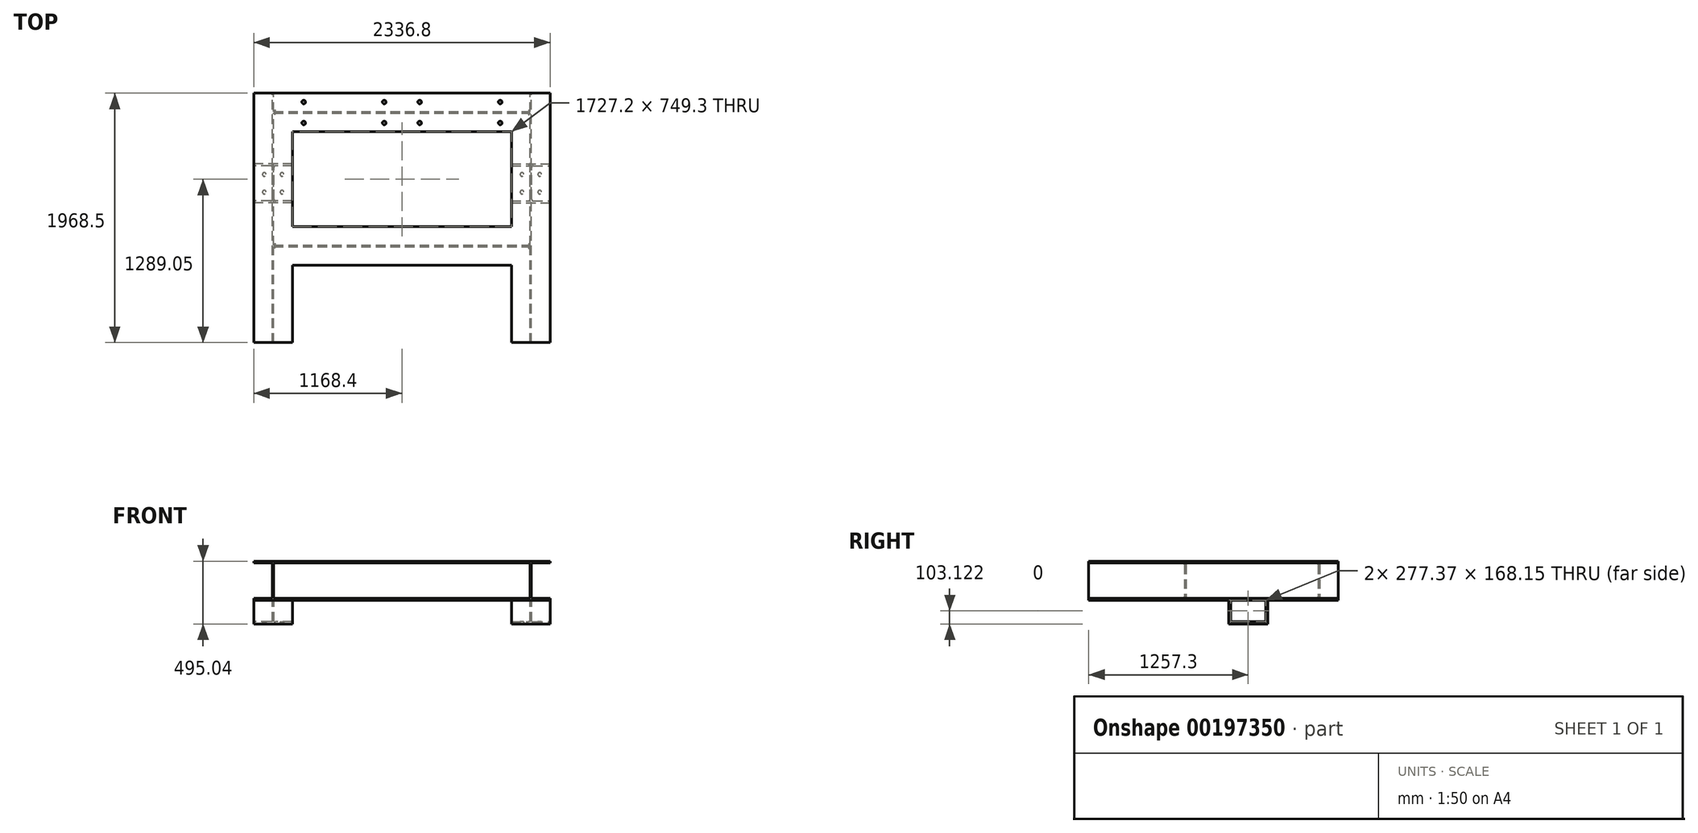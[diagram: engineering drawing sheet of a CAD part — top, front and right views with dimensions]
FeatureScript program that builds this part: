
annotation { "Feature Type Name" : "Feature", "Feature Type Description" : "" }
export const myFeature = defineFeature(function(context is Context, id is Id, definition is map)
    precondition{}
    {
        {
            var Q0;
            Q0=qCreatedBy(makeId("Front.planeOp"),FACE);
            var sketch = newSketch(context, id + "F0", { "sketchPlane" : qUnion([Q0])});
            skLineSegment(sketch, "E0", {"start": v(0, 115.72) * mm, "end": v(0, -109.56) * mm, "construction": true});
            skLineSegment(sketch, "E1", {"start": v(-1016, 0) * mm, "end": v(153.72, 0) * mm, "construction": true});
            skLineSegment(sketch, "E2.0", {"start": v(-1016, 115.72) * mm, "end": v(-1016, -109.56) * mm, "construction": true});
            skPoint(sketch, "E3.orphan", {"position": v(-192.41, 0) * mm});
            skLineSegment(sketch, "E4.bottom", {"start": v(-1168.4, -153.92) * mm, "end": v(-863.6, -153.92) * mm});
            skLineSegment(sketch, "E4.top", {"start": v(-1168.4, 153.92) * mm, "end": v(-863.6, 153.92) * mm});
            skLineSegment(sketch, "E4.left", {"start": v(-1168.4, -153.92) * mm, "end": v(-1168.4, -138.68) * mm});
            skLineSegment(sketch, "E4.right", {"start": v(-863.6, -153.92) * mm, "end": v(-863.6, -138.68) * mm});
            skPoint(sketch, "E4.middle", {"position": v(-1016, 0) * mm});
            skLineSegment(sketch, "E5.0", {"start": v(-1168.4, 138.68) * mm, "end": v(-1033.65, 138.68) * mm});
            skLineSegment(sketch, "E6.0", {"start": v(-1168.4, -138.68) * mm, "end": v(-1033.65, -138.68) * mm});
            skLineSegment(sketch, "E7.0", {"start": v(-1020.95, 125.98) * mm, "end": v(-1020.95, -125.98) * mm});
            skLineSegment(sketch, "E8.MirrorCS", {"start": v(-1011.05, 125.98) * mm, "end": v(-1011.05, -125.98) * mm});
            skPoint(sketch, "E9.orphan", {"position": v(-1020.95, 115.72) * mm});
            skPoint(sketch, "E10.orphan", {"position": v(-1011.05, 115.72) * mm});
            skPoint(sketch, "E11.orphan", {"position": v(-1020.95, -109.56) * mm});
            skPoint(sketch, "E12.orphan", {"position": v(-1011.05, -109.56) * mm});
            skLineSegment(sketch, "E13.trimOffspring", {"start": v(-998.35, 138.68) * mm, "end": v(-863.6, 138.68) * mm});
            skLineSegment(sketch, "E14.trimOffspring", {"start": v(-863.6, 138.68) * mm, "end": v(-863.6, 153.92) * mm});
            skLineSegment(sketch, "E15.trimOffspring", {"start": v(-998.35, -138.68) * mm, "end": v(-863.6, -138.68) * mm});
            skLineSegment(sketch, "E16.trimOffspring", {"start": v(-1168.4, 138.68) * mm, "end": v(-1168.4, 153.92) * mm});
            skPoint(sketch, "E17.visualSharp", {"position": v(-1020.95, 138.68) * mm});
            skArc(sketch, "E17.filletArc", {"start": v(-1020.95, 125.98) * mm, "mid": v(-1024.67, 134.96) * mm, "end": v(-1033.65, 138.68) * mm});
            skPoint(sketch, "E18.visualSharp", {"position": v(-1011.05, 138.68) * mm});
            skArc(sketch, "E18.filletArc", {"start": v(-998.35, 138.68) * mm, "mid": v(-1007.33, 134.96) * mm, "end": v(-1011.05, 125.98) * mm});
            skPoint(sketch, "E19.visualSharp", {"position": v(-1020.95, -138.68) * mm});
            skArc(sketch, "E19.filletArc", {"start": v(-1033.65, -138.68) * mm, "mid": v(-1024.67, -134.96) * mm, "end": v(-1020.95, -125.98) * mm});
            skPoint(sketch, "E20.visualSharp", {"position": v(-1011.05, -138.68) * mm});
            skArc(sketch, "E20.filletArc", {"start": v(-1011.05, -125.98) * mm, "mid": v(-1007.33, -134.96) * mm, "end": v(-998.35, -138.68) * mm});
            skSolve(sketch);
        }
        {
            var Q0;
            Q0=makeQuery(id+"F0.imprint","IMPRINT",FACE,{"disambiguationData":[TD([[makeQuery(id+"F0.imprint","IMPRINT",EDGE,{"derivedFrom":sQuery(id+"F0.wireOp",EDGE,"E4.bottom")}),1.0]])]});
            extrude(context, id + "F1", {"entities" : qUnion([Q0]), "endBound" : BoundingType.SYMMETRIC, "depth" : 1968.5 * mm});
        }
        {
            var Q0;
            Q0=qCreatedBy(makeId("Right.planeOp"),FACE);
            var sketch = newSketch(context, id + "F2", { "sketchPlane" : qUnion([Q0])});
            skLineSegment(sketch, "E21.bottom", {"start": v(984.25, 153.92) * mm, "end": v(679.45, 153.92) * mm});
            skLineSegment(sketch, "E21.top", {"start": v(984.25, -153.92) * mm, "end": v(679.45, -153.92) * mm});
            skLineSegment(sketch, "E21.left", {"start": v(984.25, 153.92) * mm, "end": v(984.25, 125.98) * mm});
            skLineSegment(sketch, "E21.right", {"start": v(679.45, 153.92) * mm, "end": v(679.45, 138.68) * mm});
            skLineSegment(sketch, "E22", {"start": v(831.85, -153.92) * mm, "end": v(831.85, 276.55) * mm, "construction": true});
            skPoint(sketch, "E22.endSnap0", {"position": v(831.85, -153.92) * mm});
            skLineSegment(sketch, "E23.0", {"start": v(-222.25, -153.92) * mm, "end": v(-222.25, 276.55) * mm, "construction": true});
            skLineSegment(sketch, "E24", {"start": v(0, 0) * mm, "end": v(-381.15, 0) * mm, "construction": true});
            skLineSegment(sketch, "E25.bottom", {"start": v(-374.65, 153.92) * mm, "end": v(-69.85, 153.92) * mm});
            skLineSegment(sketch, "E25.top", {"start": v(-374.65, -153.92) * mm, "end": v(-69.85, -153.92) * mm});
            skLineSegment(sketch, "E25.left", {"start": v(-374.65, 153.92) * mm, "end": v(-374.65, 138.68) * mm});
            skLineSegment(sketch, "E25.right", {"start": v(-69.85, 153.92) * mm, "end": v(-69.85, 125.98) * mm});
            skPoint(sketch, "E25.middle", {"position": v(-222.25, 0) * mm});
            skLineSegment(sketch, "E26.0", {"start": v(984.25, 138.68) * mm, "end": v(850.9, 138.68) * mm});
            skLineSegment(sketch, "E27.0", {"start": v(984.25, -138.68) * mm, "end": v(850.9, -138.68) * mm});
            skLineSegment(sketch, "E28.0", {"start": v(838.2, -125.98) * mm, "end": v(838.2, 125.98) * mm});
            skLineSegment(sketch, "E29.MirrorCS", {"start": v(825.5, -125.98) * mm, "end": v(825.5, 125.98) * mm});
            skPoint(sketch, "E30.orphan", {"position": v(838.2, 276.55) * mm});
            skPoint(sketch, "E31.orphan", {"position": v(825.5, 276.55) * mm});
            skPoint(sketch, "E32.orphan", {"position": v(838.2, -153.92) * mm});
            skLineSegment(sketch, "E33.trimOffspring", {"start": v(812.8, -138.68) * mm, "end": v(679.45, -138.68) * mm});
            skPoint(sketch, "E34.orphan", {"position": v(825.5, -153.92) * mm});
            skLineSegment(sketch, "E35.trimOffspring", {"start": v(812.8, 138.68) * mm, "end": v(679.45, 138.68) * mm});
            skArc(sketch, "E36.filletArc", {"start": v(825.5, 125.98) * mm, "mid": v(821.78, 134.96) * mm, "end": v(812.8, 138.68) * mm});
            skPoint(sketch, "E37.visualSharp", {"position": v(838.2, 138.68) * mm});
            skArc(sketch, "E37.filletArc", {"start": v(850.9, 138.68) * mm, "mid": v(841.92, 134.96) * mm, "end": v(838.2, 125.98) * mm});
            skPoint(sketch, "E38.visualSharp", {"position": v(838.2, -138.68) * mm});
            skArc(sketch, "E38.filletArc", {"start": v(838.2, -125.98) * mm, "mid": v(841.92, -134.96) * mm, "end": v(850.9, -138.68) * mm});
            skArc(sketch, "E39.filletArc", {"start": v(812.8, -138.68) * mm, "mid": v(821.78, -134.96) * mm, "end": v(825.5, -125.98) * mm});
            skLineSegment(sketch, "E40.trimOffspring", {"start": v(679.45, -138.68) * mm, "end": v(679.45, -153.92) * mm});
            skPoint(sketch, "E41.0.end.orphan", {"position": v(984.25, -125.98) * mm});
            skPoint(sketch, "E41.0.start.orphan", {"position": v(984.25, 125.98) * mm});
            skLineSegment(sketch, "E42.trimOffspring", {"start": v(984.25, -125.98) * mm, "end": v(984.25, -153.92) * mm});
            skLineSegment(sketch, "E43.1.0.0", {"start": v(-241.3, -138.68) * mm, "end": v(-374.65, -138.68) * mm});
            skLineSegment(sketch, "E43.1.0.1", {"start": v(-69.85, -138.68) * mm, "end": v(-203.2, -138.68) * mm});
            skPoint(sketch, "E43.1.0.2", {"position": v(-69.85, -125.98) * mm});
            skPoint(sketch, "E43.1.0.3", {"position": v(-228.6, -153.92) * mm});
            skPoint(sketch, "E43.1.0.4", {"position": v(-215.9, 138.68) * mm});
            skPoint(sketch, "E43.1.0.5", {"position": v(-215.9, -153.92) * mm});
            skLineSegment(sketch, "E43.1.0.6", {"start": v(-241.3, 138.68) * mm, "end": v(-374.65, 138.68) * mm});
            skLineSegment(sketch, "E43.1.0.7", {"start": v(-215.9, -125.98) * mm, "end": v(-215.9, 125.98) * mm});
            skLineSegment(sketch, "E43.1.0.8", {"start": v(-228.6, -125.98) * mm, "end": v(-228.6, 125.98) * mm});
            skPoint(sketch, "E43.1.0.9", {"position": v(-69.85, 125.98) * mm});
            skLineSegment(sketch, "E43.1.0.10", {"start": v(-69.85, 138.68) * mm, "end": v(-203.2, 138.68) * mm});
            skPoint(sketch, "E43.1.0.11", {"position": v(-215.9, -138.68) * mm});
            skPoint(sketch, "E43.1.0.12", {"position": v(-222.25, -153.92) * mm});
            skArc(sketch, "E43.1.0.13", {"start": v(-228.6, 125.98) * mm, "mid": v(-232.32, 134.96) * mm, "end": v(-241.3, 138.68) * mm});
            skArc(sketch, "E43.1.0.14", {"start": v(-203.2, 138.68) * mm, "mid": v(-212.18, 134.96) * mm, "end": v(-215.9, 125.98) * mm});
            skArc(sketch, "E43.1.0.15", {"start": v(-215.9, -125.98) * mm, "mid": v(-212.18, -134.96) * mm, "end": v(-203.2, -138.68) * mm});
            skArc(sketch, "E43.1.0.16", {"start": v(-241.3, -138.68) * mm, "mid": v(-232.32, -134.96) * mm, "end": v(-228.6, -125.98) * mm});
            skLineSegment(sketch, "E43.direction1", {"start": v(-69.85, -138.68) * mm, "end": v(-374.65, -138.68) * mm, "construction": true});
            skLineSegment(sketch, "E44.trimOffspring", {"start": v(-69.85, -125.98) * mm, "end": v(-69.85, -153.92) * mm});
            skLineSegment(sketch, "E45", {"start": v(-374.65, -138.68) * mm, "end": v(-374.65, -153.92) * mm});
            skSolve(sketch);
        }
        {
            var Q0;
            Q0 = qSketchRegion(id + "F2", true);
            var Q1;
            Q1=makeQuery(id+"F1.opExtrude","SWEPT_FACE",FACE,{"disambiguationData":[OSD([sQuery(id+"F0.wireOp",EDGE,"E8.MirrorCS")])]});
            extrude(context, id + "F3", {"entities" : qUnion([Q0]), "operationType" : NewBodyOperationType.ADD, "endBound" : BoundingType.UP_TO_SURFACE, "oppositeDirection" : true, "endBoundEntityFace" : qUnion([Q1]), "depth" : 25.4 * mm});
        }
        {
            var Q0;
            Q0=makeQuery(id+"F3.boolean.opBoolean","MERGE",FACE,{"derivedFrom":[makeQuery(id+"F1.opExtrude","SWEPT_FACE",FACE,{"disambiguationData":[OSD([sQuery(id+"F0.wireOp",EDGE,"E4.bottom")])]}),makeQuery(id+"F3.opExtrude","SWEPT_FACE",FACE,{"disambiguationData":[OSD([sQuery(id+"F2.wireOp",EDGE,"E21.top")])]}),makeQuery(id+"F3.opExtrude","SWEPT_FACE",FACE,{"disambiguationData":[OSD([sQuery(id+"F2.wireOp",EDGE,"E25.top")])]})]});
            var sketch = newSketch(context, id + "F4", { "sketchPlane" : qUnion([Q0])});
            skLineSegment(sketch, "E46.0", {"start": v(-1168.4, -984.25) * mm, "end": v(0, -984.25) * mm, "construction": true});
            skLineSegment(sketch, "E47.0", {"start": v(-1168.4, -273.05) * mm, "end": v(-863.6, -273.05) * mm, "construction": true});
            skLineSegment(sketch, "E48.0", {"start": v(-863.6, 69.85) * mm, "end": v(-863.6, -134.37) * mm, "construction": true});
            skLineSegment(sketch, "E49.0", {"start": v(-1168.4, 984.25) * mm, "end": v(-1168.4, -134.37) * mm, "construction": true});
            skLineSegment(sketch, "E50.bottom", {"start": v(-863.6, -119.13) * mm, "end": v(-1168.4, -119.13) * mm});
            skLineSegment(sketch, "E50.top", {"start": v(-863.6, -426.97) * mm, "end": v(-1168.4, -426.97) * mm});
            skLineSegment(sketch, "E50.left", {"start": v(-863.6, -119.13) * mm, "end": v(-863.6, -134.37) * mm});
            skLineSegment(sketch, "E50.right", {"start": v(-1168.4, -119.13) * mm, "end": v(-1168.4, -134.37) * mm});
            skPoint(sketch, "E50.middle", {"position": v(-1016, -273.05) * mm});
            skLineSegment(sketch, "E51.0", {"start": v(-863.6, -411.73) * mm, "end": v(-996.95, -411.73) * mm});
            skLineSegment(sketch, "E52.0", {"start": v(-863.6, -134.37) * mm, "end": v(-996.95, -134.37) * mm});
            skLineSegment(sketch, "E53.trimOffspring", {"start": v(-863.6, -411.73) * mm, "end": v(-863.6, -679.45) * mm, "construction": true});
            skLineSegment(sketch, "E54.trimOffspring", {"start": v(-863.6, -411.73) * mm, "end": v(-863.6, -426.97) * mm});
            skLineSegment(sketch, "E55.trimOffspring", {"start": v(-1168.4, -411.73) * mm, "end": v(-1168.4, -984.25) * mm, "construction": true});
            skLineSegment(sketch, "E56.trimOffspring", {"start": v(-1168.4, -411.73) * mm, "end": v(-1168.4, -426.97) * mm});
            skLineSegment(sketch, "E57", {"start": v(-1016, -134.37) * mm, "end": v(-1016, -411.73) * mm, "construction": true});
            skLineSegment(sketch, "E58.0", {"start": v(-1022.35, -147.07) * mm, "end": v(-1022.35, -399.03) * mm});
            skLineSegment(sketch, "E59.MirrorCS", {"start": v(-1009.65, -147.07) * mm, "end": v(-1009.65, -399.03) * mm});
            skLineSegment(sketch, "E60.trimOffspring", {"start": v(-1035.05, -134.37) * mm, "end": v(-1168.4, -134.37) * mm});
            skLineSegment(sketch, "E61.trimOffspring", {"start": v(-1035.05, -411.73) * mm, "end": v(-1168.4, -411.73) * mm});
            skPoint(sketch, "E62.visualSharp", {"position": v(-1009.65, -411.73) * mm});
            skArc(sketch, "E62.filletArc", {"start": v(-1009.65, -399.03) * mm, "mid": v(-1005.93, -408.01) * mm, "end": v(-996.95, -411.73) * mm});
            skPoint(sketch, "E63.newPointA", {"position": v(-1022.35, -411.73) * mm});
            skArc(sketch, "E63.filletArc", {"start": v(-1035.05, -411.73) * mm, "mid": v(-1026.07, -408.01) * mm, "end": v(-1022.35, -399.03) * mm});
            skPoint(sketch, "E64.visualSharp", {"position": v(-1022.35, -134.37) * mm});
            skArc(sketch, "E64.filletArc", {"start": v(-1022.35, -147.07) * mm, "mid": v(-1026.07, -138.09) * mm, "end": v(-1035.05, -134.37) * mm});
            skPoint(sketch, "E65.newPointA", {"position": v(-1009.65, -134.37) * mm});
            skArc(sketch, "E65.filletArc", {"start": v(-996.95, -134.37) * mm, "mid": v(-1005.93, -138.09) * mm, "end": v(-1009.65, -147.07) * mm});
            skSolve(sketch);
        }
        {
            var Q0;
            Q0 = qSketchRegion(id + "F4", true);
            extrude(context, id + "F5", {"entities" : qUnion([Q0]), "operationType" : NewBodyOperationType.ADD, "depth" : 168.15 * mm});
        }
        {
            var Q0;
            Q0=makeQuery(id+"F5.opExtrude","CAP_FACE",FACE,{"disambiguationData":[OSD([sQuery(id+"F4.wireOp",EDGE,"E50.bottom"),sQuery(id+"F4.wireOp",EDGE,"E50.top"),sQuery(id+"F4.wireOp",EDGE,"E50.left"),sQuery(id+"F4.wireOp",EDGE,"E50.right"),sQuery(id+"F4.wireOp",EDGE,"E51.0"),sQuery(id+"F4.wireOp",EDGE,"E52.0"),sQuery(id+"F4.wireOp",EDGE,"E54.trimOffspring"),sQuery(id+"F4.wireOp",EDGE,"E56.trimOffspring"),sQuery(id+"F4.wireOp",EDGE,"E58.0"),sQuery(id+"F4.wireOp",EDGE,"E59.MirrorCS"),sQuery(id+"F4.wireOp",EDGE,"E60.trimOffspring"),sQuery(id+"F4.wireOp",EDGE,"E61.trimOffspring"),sQuery(id+"F4.wireOp",EDGE,"E62.filletArc"),sQuery(id+"F4.wireOp",EDGE,"E63.filletArc"),sQuery(id+"F4.wireOp",EDGE,"E64.filletArc"),sQuery(id+"F4.wireOp",EDGE,"E65.filletArc")])],"isStart":false});
            var sketch = newSketch(context, id + "F6", { "sketchPlane" : qUnion([Q0])});
            skLineSegment(sketch, "E66.0", {"start": v(-863.6, -119.13) * mm, "end": v(-1168.4, -119.13) * mm});
            skLineSegment(sketch, "E67.0", {"start": v(-863.6, -426.97) * mm, "end": v(-1168.4, -426.97) * mm});
            skLineSegment(sketch, "E68.left", {"start": v(-863.6, -119.13) * mm, "end": v(-863.6, -426.97) * mm});
            skLineSegment(sketch, "E68.right", {"start": v(-1168.4, -119.13) * mm, "end": v(-1168.4, -426.97) * mm});
            skSolve(sketch);
        }
        {
            var Q0;
            Q0 = qSketchRegion(id + "F6", true);
            extrude(context, id + "F7", {"entities" : qUnion([Q0]), "operationType" : NewBodyOperationType.ADD, "depth" : 19.05 * mm});
        }
        {
            var Q0;
            Q0=makeQuery(id+"F7.opExtrude","CAP_FACE",FACE,{"disambiguationData":[OSD([sQuery(id+"F6.wireOp",EDGE,"E66.0"),sQuery(id+"F6.wireOp",EDGE,"E67.0"),sQuery(id+"F6.wireOp",EDGE,"E68.left"),sQuery(id+"F6.wireOp",EDGE,"E68.right")])],"isStart":false});
            var sketch = newSketch(context, id + "F8", { "sketchPlane" : qUnion([Q0])});
            skLineSegment(sketch, "E69", {"start": v(-1016, -119.13) * mm, "end": v(-1016, -426.97) * mm, "construction": true});
            skLineSegment(sketch, "E70", {"start": v(-863.6, -273.05) * mm, "end": v(-1168.4, -273.05) * mm, "construction": true});
            skLineSegment(sketch, "E71.0", {"start": v(-863.6, -203.2) * mm, "end": v(-1168.4, -203.2) * mm, "construction": true});
            skLineSegment(sketch, "E72.0", {"start": v(-1085.85, -119.13) * mm, "end": v(-1085.85, -426.97) * mm, "construction": true});
            skPoint(sketch, "E73", {"position": v(-1085.85, -203.2) * mm});
            skPoint(sketch, "E74.MirrorP", {"position": v(-946.15, -203.2) * mm});
            skPoint(sketch, "E75.MirrorP", {"position": v(-946.15, -342.9) * mm});
            skPoint(sketch, "E76.MirrorP", {"position": v(-1085.85, -342.9) * mm});
            skSolve(sketch);
        }
        {
            var Q0;
            Q0=sQuery(id+"F8.wireOp",VERTEX,"E74.MirrorP");
            var Q1;
            Q1=sQuery(id+"F8.wireOp",VERTEX,"E75.MirrorP");
            var Q2;
            Q2=sQuery(id+"F8.wireOp",VERTEX,"E76.MirrorP");
            var Q3;
            Q3=sQuery(id+"F8.wireOp",VERTEX,"E73");
            var Q4;
            Q4=makeQuery(id+"F1.opExtrude","SWEPT_BODY",BODY,{"disambiguationData":[OSD([sQuery(id+"F0.wireOp",EDGE,"E4.bottom"),sQuery(id+"F0.wireOp",EDGE,"E4.top"),sQuery(id+"F0.wireOp",EDGE,"E4.left"),sQuery(id+"F0.wireOp",EDGE,"E4.right"),sQuery(id+"F0.wireOp",EDGE,"E5.0"),sQuery(id+"F0.wireOp",EDGE,"E6.0"),sQuery(id+"F0.wireOp",EDGE,"E7.0"),sQuery(id+"F0.wireOp",EDGE,"E8.MirrorCS"),sQuery(id+"F0.wireOp",EDGE,"E13.trimOffspring"),sQuery(id+"F0.wireOp",EDGE,"E14.trimOffspring"),sQuery(id+"F0.wireOp",EDGE,"E15.trimOffspring"),sQuery(id+"F0.wireOp",EDGE,"E16.trimOffspring"),sQuery(id+"F0.wireOp",EDGE,"E17.filletArc"),sQuery(id+"F0.wireOp",EDGE,"E18.filletArc"),sQuery(id+"F0.wireOp",EDGE,"E19.filletArc"),sQuery(id+"F0.wireOp",EDGE,"E20.filletArc")])]});
            hole(context, id + "F9", {"style" : HoleStyle.SIMPLE, "endStyle" : HoleEndStyle.BLIND, "holeDiameter" : 28.57 * mm, "holeDepth" : 76.2 * mm, "locations" : qUnion([Q0, Q1, Q2, Q3]), "scope" : qUnion([Q4])});
        }
        {
            var Q0;
            Q0=makeQuery(id+"F3.boolean.opBoolean","MERGE",FACE,{"derivedFrom":[makeQuery(id+"F1.opExtrude","SWEPT_FACE",FACE,{"disambiguationData":[OSD([sQuery(id+"F0.wireOp",EDGE,"E4.top")])]}),makeQuery(id+"F3.opExtrude","SWEPT_FACE",FACE,{"disambiguationData":[OSD([sQuery(id+"F2.wireOp",EDGE,"E21.bottom")])]}),makeQuery(id+"F3.opExtrude","SWEPT_FACE",FACE,{"disambiguationData":[OSD([sQuery(id+"F2.wireOp",EDGE,"E25.bottom")])]})]});
            var sketch = newSketch(context, id + "F10", { "sketchPlane" : qUnion([Q0])});
            skLineSegment(sketch, "E77.0", {"start": v(-1168.4, 984.25) * mm, "end": v(0, 984.25) * mm, "construction": true});
            skLineSegment(sketch, "E78.0", {"start": v(0, 984.25) * mm, "end": v(0, 679.45) * mm, "construction": true});
            skLineSegment(sketch, "E79.0", {"start": v(-1168.4, 914.4) * mm, "end": v(0, 914.4) * mm, "construction": true});
            skLineSegment(sketch, "E80.0", {"start": v(-1168.4, 749.3) * mm, "end": v(0, 749.3) * mm, "construction": true});
            skLineSegment(sketch, "E81.0", {"start": v(-139.7, 984.25) * mm, "end": v(-139.7, 679.45) * mm, "construction": true});
            skLineSegment(sketch, "E82.0", {"start": v(-774.7, 984.25) * mm, "end": v(-774.7, 679.45) * mm, "construction": true});
            skPoint(sketch, "E83", {"position": v(-139.7, 914.4) * mm});
            skPoint(sketch, "E84", {"position": v(-139.7, 749.3) * mm});
            skPoint(sketch, "E85", {"position": v(-774.7, 749.3) * mm});
            skPoint(sketch, "E86", {"position": v(-774.7, 914.4) * mm});
            skSolve(sketch);
        }
        {
            var Q0;
            Q0=sQuery(id+"F10.wireOp",VERTEX,"E86");
            var Q1;
            Q1=sQuery(id+"F10.wireOp",VERTEX,"E85");
            var Q2;
            Q2=sQuery(id+"F10.wireOp",VERTEX,"E83");
            var Q3;
            Q3=sQuery(id+"F10.wireOp",VERTEX,"E84");
            var Q4;
            Q4=makeQuery(id+"F1.opExtrude","SWEPT_BODY",BODY,{"disambiguationData":[OSD([sQuery(id+"F0.wireOp",EDGE,"E4.bottom"),sQuery(id+"F0.wireOp",EDGE,"E4.top"),sQuery(id+"F0.wireOp",EDGE,"E4.left"),sQuery(id+"F0.wireOp",EDGE,"E4.right"),sQuery(id+"F0.wireOp",EDGE,"E5.0"),sQuery(id+"F0.wireOp",EDGE,"E6.0"),sQuery(id+"F0.wireOp",EDGE,"E7.0"),sQuery(id+"F0.wireOp",EDGE,"E8.MirrorCS"),sQuery(id+"F0.wireOp",EDGE,"E13.trimOffspring"),sQuery(id+"F0.wireOp",EDGE,"E14.trimOffspring"),sQuery(id+"F0.wireOp",EDGE,"E15.trimOffspring"),sQuery(id+"F0.wireOp",EDGE,"E16.trimOffspring"),sQuery(id+"F0.wireOp",EDGE,"E17.filletArc"),sQuery(id+"F0.wireOp",EDGE,"E18.filletArc"),sQuery(id+"F0.wireOp",EDGE,"E19.filletArc"),sQuery(id+"F0.wireOp",EDGE,"E20.filletArc")])]});
            hole(context, id + "F11", {"style" : HoleStyle.SIMPLE, "endStyle" : HoleEndStyle.BLIND, "holeDiameter" : 28.57 * mm, "holeDepth" : 76.2 * mm, "locations" : qUnion([Q0, Q1, Q2, Q3]), "scope" : qUnion([Q4])});
        }
        {
            var Q0;
            Q0=makeQuery(id+"F1.opExtrude","SWEPT_BODY",BODY,{"disambiguationData":[OSD([sQuery(id+"F0.wireOp",EDGE,"E4.bottom"),sQuery(id+"F0.wireOp",EDGE,"E4.top"),sQuery(id+"F0.wireOp",EDGE,"E4.left"),sQuery(id+"F0.wireOp",EDGE,"E4.right"),sQuery(id+"F0.wireOp",EDGE,"E5.0"),sQuery(id+"F0.wireOp",EDGE,"E6.0"),sQuery(id+"F0.wireOp",EDGE,"E7.0"),sQuery(id+"F0.wireOp",EDGE,"E8.MirrorCS"),sQuery(id+"F0.wireOp",EDGE,"E13.trimOffspring"),sQuery(id+"F0.wireOp",EDGE,"E14.trimOffspring"),sQuery(id+"F0.wireOp",EDGE,"E15.trimOffspring"),sQuery(id+"F0.wireOp",EDGE,"E16.trimOffspring"),sQuery(id+"F0.wireOp",EDGE,"E17.filletArc"),sQuery(id+"F0.wireOp",EDGE,"E18.filletArc"),sQuery(id+"F0.wireOp",EDGE,"E19.filletArc"),sQuery(id+"F0.wireOp",EDGE,"E20.filletArc")])]});
            var Q1;
            Q1=qCreatedBy(makeId("Right.planeOp"),FACE);
            mirror(context, id + "F12", {"operationType" : NewBodyOperationType.ADD, "entities" : qUnion([Q0]), "mirrorPlane" : qUnion([Q1])});
        }
    });
